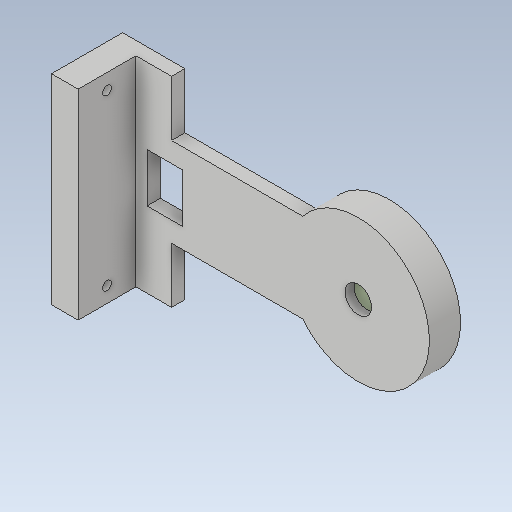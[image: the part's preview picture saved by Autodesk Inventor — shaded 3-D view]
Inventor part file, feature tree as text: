
AUTODESK INVENTOR PART (.ipt)
format: ipt  version: 2020 (Build 240168000, 168)  size: 185,856 bytes
history: native  units: mm
features: extrude x9, sketch x9, other x3, plane x1, hole x1, reference x1
ambient origin geometry x8: Origin, YZ Plane, XZ Plane, XY Plane, X Axis, Y Axis, Z Axis, Center Point
bodies: Solid1 (feature_tree)
feature tree (24):
  extrude  "Extrusion1"  Depth=7.0mm
  extrude  "Extrusion3"  Depth=3.0mm TaperAngle=0.0deg
  sketch  "Sketch5"  dims[d10=45.0mm d11=16.0mm]
  extrude  "Extrusion4"  Depth=16.0mm
  extrude  "Extrusion5"  Depth=3.0mm TaperAngle=0.0deg
  extrude  "Extrusion6"  Depth=8.0mm
  extrude  "Extrusion7"  Depth=2.5mm
  extrude  "Extrusion8"  Depth=11.0mm
  plane  "Work Plane1"
  extrude  "Extrusion11"  Depth=2.0mm
  hole  "Hole1"  [1 undecoded]
  extrude  "Extrusion12"  Depth=5.0mm
  sketch  "Sketch1"  dims[d0=7.0mm d1=0.0mm d6=50.0mm]
  reference  "Reference1"
  sketch  "Sketch4"  dims[d7=10.0mm d8=3.0mm d9=0.0mm]
  sketch  "Sketch6"  dims[d12=16.0mm d13=3.0mm d14=0.0mm]
  sketch  "Sketch7"  dims[d15=3.0mm d16=0.0mm d17=8.0mm]
  sketch  "Sketch8"  dims[d18=13.0mm d19=0.0mm d20=2.5mm]
  sketch  "Sketch12"  dims[d21=8.0mm d22=11.0mm]
  sketch  "Sketch13"  dims[d23=13.0mm d24=0.0mm d25=2.0mm]
  sketch  "Sketch14"  dims[d26=13.0mm d27=0.0mm d35=1.0mm d36=0.0mm d37=3.5mm d38=3.5mm d39=2.0mm d40=6.0mm d41=4.0mm d42=2.0mm d43=90.0deg d44=5.0mm d45=20.594885mm d46=6.0mm d47=14.0mm d48=5.0mm d49=0.0mm]
  other  "<userpath>\Desktop\3d\scanning-robot\Assembly1.iam"
  other  "Assembly1.iam"
  other  "cover:1"
note: 1 required parameter value undecoded (feature->parameter linkage not recoverable at this tier; creation-order binding heuristic only, values carry confidence <= 0.55)
